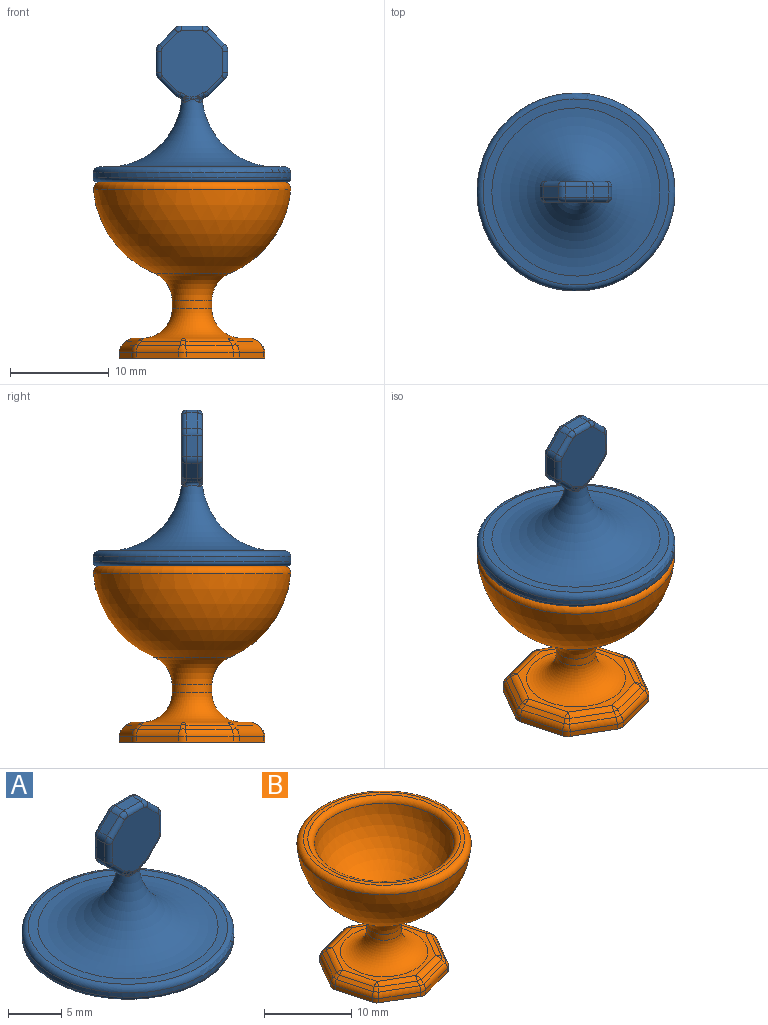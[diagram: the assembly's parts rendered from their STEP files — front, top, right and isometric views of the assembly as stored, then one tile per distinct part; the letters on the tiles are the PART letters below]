
ASSEMBLY  parts=2 mates=1
PART A: 83 faces, bbox 22.1x22.1x17.3 mm
  f0: torus R=8.5mm, axis (0,0,-1), area 155.4mm2, adj f18
  f1: cylinder r=6.8mm len=13.6mm, axis (0,0,-1), area 11.7mm2, adj f18,f19
  f2: plane 14.8x14.8mm, normal (0,0,-1), area 9.2mm2, adj f19,f20
  f3: cylinder r=7.8mm len=15.6mm, axis (0,0,-1), area 9.8mm2, adj f20,f21
  f4: plane 19.2x19.2mm, normal (0,0,-1), area 78.3mm2, adj f21,f22
  f5: cylinder r=10mm len=20mm, axis (0,0,-1), area 31.4mm2, adj f17,f22
  f6: plane 18.8x18.8mm, normal (0,0,1), area 50.6mm2, adj f7,f17
  f7: torus R=8.5mm, axis (0,0,-1), area 270.2mm2, adj f6,f31,f32,f33,f34,f35,f36,f37
  f8: plane 1.54x1.54mm, normal (0.71,0,-0.71), area 2.4mm2, adj f23,f24,f39,f61
  f9: plane 2.17x1.1mm, normal (1,0,0), area 2.4mm2, adj f24,f25,f42,f65
  f10: plane 1.54x1.54mm, normal (0.71,0,0.71), area 2.4mm2, adj f25,f26,f46,f69
  f11: plane 2.17x1.1mm, normal (0,0,1), area 2.4mm2, adj f26,f27,f50,f73
  f12: plane 1.54x1.54mm, normal (-0.71,0,0.71), area 2.4mm2, adj f27,f28,f54,f77
  f13: plane 2.17x1.1mm, normal (-1,0,0), area 2.4mm2, adj f28,f29,f58,f81
  f14: plane 1.54x1.54mm, normal (-0.71,0,-0.71), area 2.4mm2, adj f29,f30,f59,f80
  f15: plane 7.17x6.74mm, normal (0,-1,0), area 32.8mm2, adj f39,f40,f41,f42,f43,f44,f45,f46
  f16: plane 7.05x6.62mm, normal (0,1,0), area 32.8mm2, adj f61,f62,f63,f64,f65,f66,f67,f69
  f17: torus R=9.4mm, axis (0,0,1), area 57.9mm2, adj f5,f6
  f18: torus R=6.4mm, axis (0,0,-1), area 22.7mm2, adj f0,f1
  f19: torus R=7.2mm, axis (0,0,-1), area 27.4mm2, adj f1,f2
  f20: torus R=7.4mm, axis (0,0,-1), area 30.2mm2, adj f2,f3
  f21: torus R=8.2mm, axis (0,0,-1), area 31.4mm2, adj f3,f4
  f22: torus R=9.6mm, axis (0,0,-1), area 38.9mm2, adj f4,f5
  f23: cylinder r=1mm len=1.1mm, axis (0,1,0), area 0.6mm2, adj f8,f31,f41,f62
  f24: cylinder r=1mm len=1.1mm, axis (0,1,0), area 0.9mm2, adj f8,f9,f40,f63
  f25: cylinder r=1mm len=1.1mm, axis (0,1,0), area 0.9mm2, adj f9,f10,f44,f67
  f26: cylinder r=1mm len=1.1mm, axis (0,1,0), area 0.9mm2, adj f10,f11,f48,f71
  f27: cylinder r=1mm len=1.1mm, axis (0,1,0), area 0.9mm2, adj f11,f12,f52,f75
  f28: cylinder r=1mm len=1.1mm, axis (0,1,0), area 0.9mm2, adj f12,f13,f56,f79
  f29: cylinder r=1mm len=1.1mm, axis (0,1,0), area 0.9mm2, adj f13,f14,f60,f82
  f30: cylinder r=1mm len=1.1mm, axis (0,1,0), area 0.6mm2, adj f14,f38,f57,f78
  f31: bspline ~2.28x0.69mm, area 0.9mm2, adj f7,f23,f32,f33,f43,f64
  f32: torus R=1.46mm, axis (0,0,1), area 0mm2, adj f7,f31,f34,f66
  f33: torus R=1.46mm, axis (0,0,1), area 0mm2, adj f7,f31,f35,f45
  f34: bspline ~2.1x0.49mm, area 0.3mm2, adj f7,f32,f36,f68,f70,f72
  f35: bspline ~2.1x0.49mm, area 0.3mm2, adj f7,f33,f37,f47,f49,f51
  f36: torus R=1.46mm, axis (0,0,1), area 0mm2, adj f7,f34,f38,f74
  f37: torus R=1.46mm, axis (0,0,1), area 0mm2, adj f7,f35,f38,f53
  f38: bspline ~2.28x0.69mm, area 0.9mm2, adj f7,f30,f36,f37,f55,f76
  f39: cylinder r=0.5mm len=1.89mm, axis (-0.71,0,-0.71), area 1.7mm2, adj f8,f15,f40,f41
  f40: torus R=0.5mm, axis (0,-1,0), area 0.5mm2, adj f15,f24,f39,f42
  f41: torus R=0.5mm, axis (0,-1,0), area 0.4mm2, adj f15,f23,f39,f43
  f42: cylinder r=0.5mm len=2.17mm, axis (0,0,-1), area 1.7mm2, adj f9,f15,f40,f44
  f43: bspline ~0.75x0.65mm, area 0.3mm2, adj f15,f31,f41,f45
  f44: torus R=0.5mm, axis (0,-1,0), area 0.5mm2, adj f15,f25,f42,f46
  f45: bspline ~0.52x0.49mm, area 0mm2, adj f15,f33,f43,f47
  f46: cylinder r=0.5mm len=1.89mm, axis (0.71,0,-0.71), area 1.7mm2, adj f10,f15,f44,f48
  f47: bspline ~0.35x0.27mm, area 0mm2, adj f15,f35,f45,f49
  f48: torus R=0.5mm, axis (0,-1,0), area 0.5mm2, adj f15,f26,f46,f50
  f49: bspline ~1.39x0.31mm, area 1mm2, adj f15,f35,f47,f51
  f50: cylinder r=0.5mm len=2.17mm, axis (1,0,0), area 1.7mm2, adj f11,f15,f48,f52
  f51: bspline ~0.34x0.25mm, area 0mm2, adj f35,f49,f53
  f52: torus R=0.5mm, axis (0,-1,0), area 0.5mm2, adj f15,f27,f50,f54
  f53: bspline ~0.52x0.49mm, area 0mm2, adj f15,f37,f51,f55
  f54: cylinder r=0.5mm len=1.89mm, axis (0.71,0,0.71), area 1.7mm2, adj f12,f15,f52,f56
  f55: bspline ~0.8x0.65mm, area 0.3mm2, adj f15,f38,f53,f57
  f56: torus R=0.5mm, axis (0,-1,0), area 0.5mm2, adj f15,f28,f54,f58
  f57: torus R=0.5mm, axis (0,-1,0), area 0.4mm2, adj f15,f30,f55,f59
  f58: cylinder r=0.5mm len=2.17mm, axis (0,0,1), area 1.7mm2, adj f13,f15,f56,f60
  f59: cylinder r=0.5mm len=1.89mm, axis (-0.71,0,0.71), area 1.7mm2, adj f14,f15,f57,f60
  f60: torus R=0.5mm, axis (0,-1,0), area 0.5mm2, adj f15,f29,f58,f59
  f61: cylinder r=0.5mm len=1.89mm, axis (0.71,0,0.71), area 1.7mm2, adj f8,f16,f62,f63
  f62: torus R=0.5mm, axis (0,-1,0), area 0.4mm2, adj f16,f23,f61,f64
  f63: torus R=0.5mm, axis (0,-1,0), area 0.5mm2, adj f16,f24,f61,f65
  f64: bspline ~0.8x0.65mm, area 0.3mm2, adj f16,f31,f62,f66
  f65: cylinder r=0.5mm len=2.17mm, axis (0,0,1), area 1.7mm2, adj f9,f16,f63,f67
  f66: bspline ~0.52x0.49mm, area 0mm2, adj f16,f32,f64,f68
  f67: torus R=0.5mm, axis (0,-1,0), area 0.5mm2, adj f16,f25,f65,f69
  f68: bspline ~0.34x0.25mm, area 0mm2, adj f34,f66,f70
  f69: cylinder r=0.5mm len=1.89mm, axis (-0.71,0,0.71), area 1.7mm2, adj f10,f16,f67,f71
  f70: bspline ~1.39x0.31mm, area 30.6mm2, adj f16,f34,f68,f72
  f71: torus R=0.5mm, axis (0,-1,0), area 0.5mm2, adj f16,f26,f69,f73
  f72: bspline ~0.35x0.27mm, area 0mm2, adj f16,f34,f70,f74
  f73: cylinder r=0.5mm len=2.17mm, axis (-1,0,0), area 1.7mm2, adj f11,f16,f71,f75
  f74: bspline ~0.52x0.49mm, area 0mm2, adj f16,f36,f72,f76
  f75: torus R=0.5mm, axis (0,-1,0), area 0.5mm2, adj f16,f27,f73,f77
  f76: bspline ~0.75x0.65mm, area 0.3mm2, adj f16,f38,f74,f78
  f77: cylinder r=0.5mm len=1.89mm, axis (-0.71,0,-0.71), area 1.7mm2, adj f12,f16,f75,f79
  f78: torus R=0.5mm, axis (0,-1,0), area 0.4mm2, adj f16,f30,f76,f80
  f79: torus R=0.5mm, axis (0,-1,0), area 0.5mm2, adj f16,f28,f77,f81
  f80: cylinder r=0.5mm len=1.89mm, axis (0.71,0,-0.71), area 1.7mm2, adj f14,f16,f78,f82
  f81: cylinder r=0.5mm len=2.17mm, axis (0,0,-1), area 1.7mm2, adj f13,f16,f79,f82
  f82: torus R=0.5mm, axis (0,-1,0), area 0.5mm2, adj f16,f29,f80,f81
PART B: 74 faces, bbox 21.6x21.6x17.8 mm
  f0: cylinder r=2mm len=4mm, axis (0,0,1), area 10mm2, adj f14,f15
  f1: sphere r=10mm, area 529mm2, adj f15,f72
  f2: plane 18.44x18.44mm, normal (0,0,1), area 28.3mm2, adj f72,f73
  f3: sphere r=8mm, area 367.7mm2, adj f73
  f4: plane 4.25x2.47mm, normal (0.86,-0.5,0), area 2.9mm2, adj f12,f24,f28,f43
  f5: plane 4.75x1.26mm, normal (0.26,-0.97,0), area 2.9mm2, adj f12,f24,f26,f47
  f6: plane 4.25x2.47mm, normal (-0.5,-0.86,0), area 2.9mm2, adj f12,f26,f30,f51
  f7: plane 4.75x1.26mm, normal (-0.97,-0.26,0), area 2.9mm2, adj f12,f30,f34,f55
  f8: plane 4.25x2.47mm, normal (-0.86,0.5,0), area 2.9mm2, adj f12,f34,f38,f52
  f9: plane 4.75x1.26mm, normal (-0.26,0.97,0), area 2.9mm2, adj f12,f36,f38,f48
  f10: plane 4.25x2.47mm, normal (0.5,0.86,0), area 2.9mm2, adj f12,f32,f36,f44
  f11: plane 4.75x1.26mm, normal (0.97,0.26,0), area 2.9mm2, adj f12,f28,f32,f40
  f12: plane 14.72x14.72mm, normal (0,0,-1), area 158.9mm2, adj f4,f5,f6,f7,f8,f9,f10,f11
  f13: plane 11.83x11.83mm, normal (0,0,1), area 22.2mm2, adj f14,f56,f59,f60,f63,f64,f67,f68
  f14: torus R=5mm, axis (0,0,-1), area 91.5mm2, adj f0,f13
  f15: torus R=5mm, axis (0,0,1), area 58.6mm2, adj f0,f1
  f16: plane 4.75x1.62mm, normal (0.18,-0.68,0.71), area 2.8mm2, adj f25,f27,f47,f64
  f17: plane 4.31x2.74mm, normal (0.61,-0.35,0.71), area 2.8mm2, adj f25,f29,f43,f60
  f18: plane 4.31x2.74mm, normal (-0.35,-0.61,0.71), area 2.8mm2, adj f27,f31,f51,f68
  f19: plane 4.75x1.62mm, normal (0.68,0.18,0.71), area 2.8mm2, adj f29,f33,f40,f56
  f20: plane 4.75x1.62mm, normal (-0.68,-0.18,0.71), area 2.8mm2, adj f31,f35,f55,f71
  f21: plane 4.31x2.74mm, normal (0.35,0.61,0.71), area 2.8mm2, adj f33,f37,f44,f59
  f22: plane 4.31x2.74mm, normal (-0.61,0.35,0.71), area 2.8mm2, adj f35,f39,f52,f67
  f23: plane 4.75x1.62mm, normal (-0.18,0.68,0.71), area 2.8mm2, adj f37,f39,f48,f63
  f24: cylinder r=1mm len=0.61mm, axis (0,0,1), area 0.5mm2, adj f4,f5,f12,f45
  f25: cylinder r=1mm len=0.7mm, axis (0.45,-0.58,-0.68), area 0.3mm2, adj f16,f17,f45,f62
  f26: cylinder r=1mm len=0.76mm, axis (0,0,1), area 0.5mm2, adj f5,f6,f12,f49
  f27: cylinder r=1mm len=0.6mm, axis (0.1,0.73,0.68), area 0.3mm2, adj f16,f18,f49,f66
  f28: cylinder r=1mm len=0.76mm, axis (0,0,1), area 0.5mm2, adj f4,f11,f12,f41
  f29: cylinder r=1mm len=0.6mm, axis (0.73,-0.1,-0.68), area 0.3mm2, adj f17,f19,f41,f58
  f30: cylinder r=1mm len=0.61mm, axis (0,0,1), area 0.5mm2, adj f6,f7,f12,f53
  f31: cylinder r=1mm len=0.7mm, axis (0.58,0.45,0.68), area 0.3mm2, adj f18,f20,f53,f70
  f32: cylinder r=1mm len=0.61mm, axis (0,0,1), area 0.5mm2, adj f10,f11,f12,f42
  f33: cylinder r=1mm len=0.7mm, axis (0.58,0.45,-0.68), area 0.3mm2, adj f19,f21,f42,f57
  f34: cylinder r=1mm len=0.76mm, axis (0,0,1), area 0.5mm2, adj f7,f8,f12,f54
  f35: cylinder r=1mm len=0.6mm, axis (0.73,-0.1,0.68), area 0.3mm2, adj f20,f22,f54,f69
  f36: cylinder r=1mm len=0.76mm, axis (0,0,1), area 0.5mm2, adj f9,f10,f12,f46
  f37: cylinder r=1mm len=0.6mm, axis (0.1,0.73,-0.68), area 0.3mm2, adj f21,f23,f46,f61
  f38: cylinder r=1mm len=0.61mm, axis (0,0,1), area 0.5mm2, adj f8,f9,f12,f50
  f39: cylinder r=1mm len=0.7mm, axis (0.45,-0.58,0.68), area 0.3mm2, adj f22,f23,f50,f65
  f40: cylinder r=1mm len=4.82mm, axis (0.26,-0.97,0), area 3.9mm2, adj f11,f19,f41,f42
  f41: sphere r=1mm, area 0.6mm2, adj f28,f29,f40,f43
  f42: sphere r=1mm, area 0.6mm2, adj f32,f33,f40,f44
  f43: cylinder r=1mm len=4.4mm, axis (-0.5,-0.86,0), area 3.9mm2, adj f4,f17,f41,f45
  f44: cylinder r=1mm len=4.4mm, axis (0.86,-0.5,0), area 3.9mm2, adj f10,f21,f42,f46
  f45: sphere r=1mm, area 0.6mm2, adj f24,f25,f43,f47
  f46: sphere r=1mm, area 0.6mm2, adj f36,f37,f44,f48
  f47: cylinder r=1mm len=4.82mm, axis (-0.97,-0.26,0), area 3.9mm2, adj f5,f16,f45,f49
  f48: cylinder r=1mm len=4.82mm, axis (0.97,0.26,0), area 3.9mm2, adj f9,f23,f46,f50
  f49: sphere r=1mm, area 0.6mm2, adj f26,f27,f47,f51
  f50: sphere r=1mm, area 0.6mm2, adj f38,f39,f48,f52
  f51: cylinder r=1mm len=4.4mm, axis (-0.86,0.5,0), area 3.9mm2, adj f6,f18,f49,f53
  f52: cylinder r=1mm len=4.4mm, axis (0.5,0.86,0), area 3.9mm2, adj f8,f22,f50,f54
  f53: sphere r=1mm, area 0.6mm2, adj f30,f31,f51,f55
  f54: sphere r=1mm, area 0.6mm2, adj f34,f35,f52,f55
  f55: cylinder r=1mm len=4.82mm, axis (-0.26,0.97,0), area 3.9mm2, adj f7,f20,f53,f54
  f56: cylinder r=1mm len=4.6mm, axis (0.26,-0.97,0), area 3.6mm2, adj f13,f19,f57,f58
  f57: sphere r=1mm, area 0.2mm2, adj f33,f56,f59
  f58: sphere r=1mm, area 0.2mm2, adj f29,f56,f60
  f59: cylinder r=1mm len=4.31mm, axis (0.86,-0.5,0), area 3.6mm2, adj f13,f21,f57,f61
  f60: cylinder r=1mm len=4.31mm, axis (-0.5,-0.86,0), area 3.6mm2, adj f13,f17,f58,f62
  f61: sphere r=1mm, area 0.2mm2, adj f37,f59,f63
  f62: sphere r=1mm, area 0.2mm2, adj f25,f60,f64
  f63: cylinder r=1mm len=4.6mm, axis (0.97,0.26,0), area 3.6mm2, adj f13,f23,f61,f65
  f64: cylinder r=1mm len=4.6mm, axis (-0.97,-0.26,0), area 3.6mm2, adj f13,f16,f62,f66
  f65: sphere r=1mm, area 0.2mm2, adj f39,f63,f67
  f66: sphere r=1mm, area 0.2mm2, adj f27,f64,f68
  f67: cylinder r=1mm len=4.31mm, axis (0.5,0.86,0), area 3.6mm2, adj f13,f22,f65,f69
  f68: cylinder r=1mm len=4.31mm, axis (-0.86,0.5,0), area 3.6mm2, adj f13,f18,f66,f70
  f69: sphere r=1mm, area 0.2mm2, adj f35,f67,f71
  f70: sphere r=1mm, area 0.2mm2, adj f31,f68,f71
  f71: cylinder r=1mm len=4.6mm, axis (-0.26,0.97,0), area 3.6mm2, adj f13,f20,f69,f70
  f72: torus R=9.22mm, axis (0,0,1), area 75.6mm2, adj f1,f2
  f73: torus R=8.72mm, axis (0,0,1), area 57.8mm2, adj f2,f3
PLACE A t=(0.38,0.54,3.71)mm
PLACE B t=(0.38,0.54,3.71)mm fixed
MATE fastened A.f0 <-> B.f72  axis (0,0,-1) through (0.38,0.54,3.71)mm
